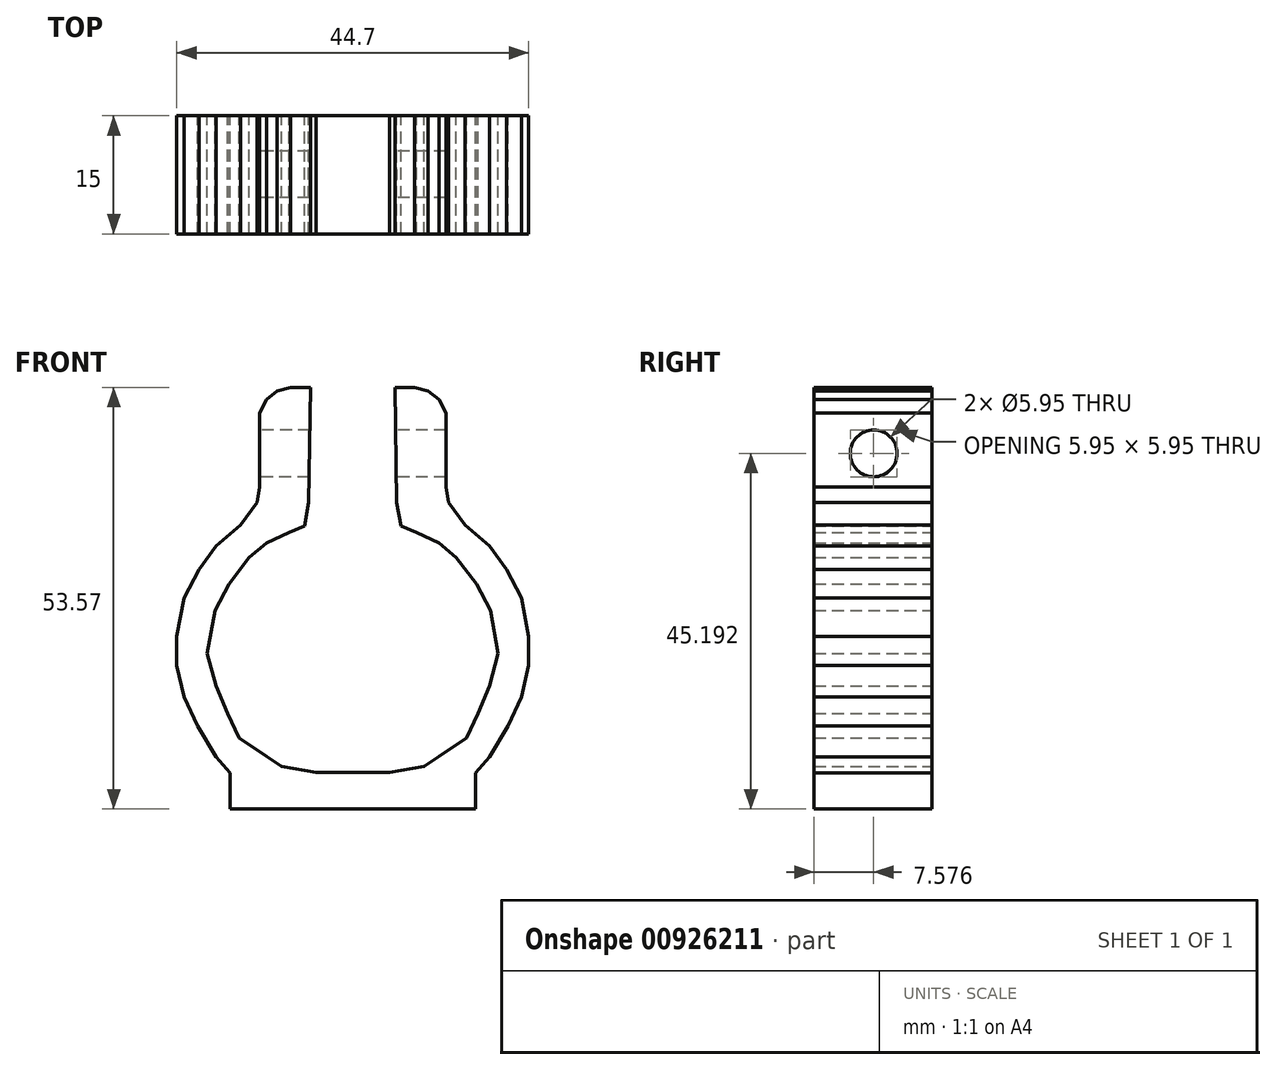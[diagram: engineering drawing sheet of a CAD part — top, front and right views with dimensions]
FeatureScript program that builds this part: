
annotation { "Feature Type Name" : "Feature", "Feature Type Description" : "" }
export const myFeature = defineFeature(function(context is Context, id is Id, definition is map)
    precondition{}
    {
        {
            var Q0;
            Q0=qCreatedBy(makeId("Front.planeOp"),FACE);
            var sketch = newSketch(context, id + "F0", { "sketchPlane" : qUnion([Q0])});
            skLineSegment(sketch, "E0", {"start": v(6.06, 26.73) * mm, "end": v(3.54, 26.73) * mm});
            skLineSegment(sketch, "E1", {"start": v(3.54, 26.73) * mm, "end": v(1.82, 26.27) * mm});
            skLineSegment(sketch, "E2", {"start": v(1.82, 26.27) * mm, "end": v(0.45, 25.22) * mm});
            skLineSegment(sketch, "E3", {"start": v(0.45, 25.22) * mm, "end": v(-0.41, 23.5) * mm});
            skLineSegment(sketch, "E4", {"start": v(-0.41, 23.5) * mm, "end": v(-0.41, 14.1) * mm});
            skLineSegment(sketch, "E5", {"start": v(-0.41, 14.1) * mm, "end": v(-0.77, 12.14) * mm});
            skLineSegment(sketch, "E6", {"start": v(-0.77, 12.14) * mm, "end": v(-2.86, 9.26) * mm});
            skLineSegment(sketch, "E7", {"start": v(-2.86, 9.26) * mm, "end": v(-5.94, 6.6) * mm});
            skLineSegment(sketch, "E8", {"start": v(-5.94, 6.6) * mm, "end": v(-8.14, 3.58) * mm});
            skLineSegment(sketch, "E9", {"start": v(-8.14, 3.58) * mm, "end": v(-10.04, 0) * mm});
            skLineSegment(sketch, "E10", {"start": v(-10.04, 0) * mm, "end": v(-10.94, -4.9) * mm});
            skLineSegment(sketch, "E11", {"start": v(-10.94, -4.9) * mm, "end": v(-10.94, -8.62) * mm});
            skLineSegment(sketch, "E12", {"start": v(-10.94, -8.62) * mm, "end": v(-10.04, -12.58) * mm});
            skLineSegment(sketch, "E13", {"start": v(-10.04, -12.58) * mm, "end": v(-8.29, -16.24) * mm});
            skLineSegment(sketch, "E14", {"start": v(-8.29, -16.24) * mm, "end": v(-5.94, -20.2) * mm});
            skLineSegment(sketch, "E15", {"start": v(-5.94, -20.2) * mm, "end": v(-4.16, -22.27) * mm});
            skLineSegment(sketch, "E16", {"start": v(-4.16, -22.27) * mm, "end": v(-4.16, -26.84) * mm});
            skLineSegment(sketch, "E17", {"start": v(-4.16, -26.84) * mm, "end": v(11.41, -26.84) * mm});
            skLineSegment(sketch, "E18", {"start": v(11.41, -22.19) * mm, "end": v(6.73, -22.19) * mm});
            skLineSegment(sketch, "E19", {"start": v(6.73, -22.19) * mm, "end": v(2.38, -21.4) * mm});
            skLineSegment(sketch, "E20", {"start": v(2.38, -21.4) * mm, "end": v(0.45, -20.13) * mm});
            skLineSegment(sketch, "E21", {"start": v(0.45, -20.13) * mm, "end": v(-3.03, -17.77) * mm});
            skLineSegment(sketch, "E22", {"start": v(-3.03, -17.77) * mm, "end": v(-4.48, -14.72) * mm});
            skLineSegment(sketch, "E23", {"start": v(-4.48, -14.72) * mm, "end": v(-5.94, -11.21) * mm});
            skLineSegment(sketch, "E24", {"start": v(-5.94, -11.21) * mm, "end": v(-7.07, -7.1) * mm});
            skLineSegment(sketch, "E25", {"start": v(-7.07, -7.1) * mm, "end": v(-6.67, -4.92) * mm});
            skLineSegment(sketch, "E26", {"start": v(-6.67, -4.92) * mm, "end": v(-6.07, -1.6) * mm});
            skLineSegment(sketch, "E27", {"start": v(-6.07, -1.6) * mm, "end": v(-4.33, 1.75) * mm});
            skLineSegment(sketch, "E28", {"start": v(-4.33, 1.75) * mm, "end": v(-1.73, 5.1) * mm});
            skLineSegment(sketch, "E29", {"start": v(-1.73, 5.1) * mm, "end": v(0.45, 6.99) * mm});
            skLineSegment(sketch, "E30", {"start": v(0.45, 6.99) * mm, "end": v(3.3, 8.3) * mm});
            skLineSegment(sketch, "E31", {"start": v(3.3, 8.3) * mm, "end": v(5.28, 9.14) * mm});
            skLineSegment(sketch, "E32", {"start": v(5.28, 9.14) * mm, "end": v(5.83, 12.14) * mm});
            skLineSegment(sketch, "E33", {"start": v(11.41, -26.84) * mm, "end": v(11.41, -22.19) * mm});
            skLineSegment(sketch, "E34", {"start": v(11.41, -31.75) * mm, "end": v(11.41, 67.33) * mm});
            skLineSegment(sketch, "E35.MirrorCS", {"start": v(30.96, 3.58) * mm, "end": v(32.86, 0) * mm});
            skLineSegment(sketch, "E36.MirrorCS", {"start": v(29.9, -7.1) * mm, "end": v(29.5, -4.92) * mm});
            skLineSegment(sketch, "E37.MirrorCS", {"start": v(28.76, -20.2) * mm, "end": v(26.98, -22.27) * mm});
            skLineSegment(sketch, "E38.MirrorCS", {"start": v(32.86, 0) * mm, "end": v(33.76, -4.9) * mm});
            skLineSegment(sketch, "E39.MirrorCS", {"start": v(28.9, -1.6) * mm, "end": v(27.15, 1.75) * mm});
            skLineSegment(sketch, "E40.MirrorCS", {"start": v(27.15, 1.75) * mm, "end": v(24.56, 5.1) * mm});
            skLineSegment(sketch, "E41.MirrorCS", {"start": v(29.5, -4.92) * mm, "end": v(28.9, -1.6) * mm});
            skLineSegment(sketch, "E42.MirrorCS", {"start": v(28.76, 6.6) * mm, "end": v(30.96, 3.58) * mm});
            skLineSegment(sketch, "E43.MirrorCS", {"start": v(28.76, -11.21) * mm, "end": v(29.9, -7.1) * mm});
            skLineSegment(sketch, "E44.MirrorCS", {"start": v(22.37, 6.99) * mm, "end": v(19.52, 8.3) * mm});
            skLineSegment(sketch, "E45.MirrorCS", {"start": v(33.76, -4.9) * mm, "end": v(33.76, -8.62) * mm});
            skLineSegment(sketch, "E46.MirrorCS", {"start": v(21, 26.27) * mm, "end": v(22.37, 25.22) * mm});
            skLineSegment(sketch, "E47.MirrorCS", {"start": v(22.37, 25.22) * mm, "end": v(23.24, 23.5) * mm});
            skLineSegment(sketch, "E48.MirrorCS", {"start": v(25.68, 9.26) * mm, "end": v(28.76, 6.6) * mm});
            skLineSegment(sketch, "E49.MirrorCS", {"start": v(23.24, 23.5) * mm, "end": v(23.24, 14.1) * mm});
            skLineSegment(sketch, "E50.MirrorCS", {"start": v(33.76, -8.62) * mm, "end": v(32.86, -12.58) * mm});
            skLineSegment(sketch, "E51.MirrorCS", {"start": v(20.44, -21.4) * mm, "end": v(22.37, -20.13) * mm});
            skLineSegment(sketch, "E52.MirrorCS", {"start": v(23.24, 14.1) * mm, "end": v(23.6, 12.14) * mm});
            skLineSegment(sketch, "E53.MirrorCS", {"start": v(27.3, -14.72) * mm, "end": v(28.76, -11.21) * mm});
            skLineSegment(sketch, "E54.MirrorCS", {"start": v(16.1, -22.19) * mm, "end": v(20.44, -21.4) * mm});
            skLineSegment(sketch, "E55.MirrorCS", {"start": v(32.86, -12.58) * mm, "end": v(31.11, -16.24) * mm});
            skLineSegment(sketch, "E56.MirrorCS", {"start": v(25.85, -17.77) * mm, "end": v(27.3, -14.72) * mm});
            skLineSegment(sketch, "E57.MirrorCS", {"start": v(31.11, -16.24) * mm, "end": v(28.76, -20.2) * mm});
            skLineSegment(sketch, "E58.MirrorCS", {"start": v(26.98, -22.27) * mm, "end": v(26.98, -26.84) * mm});
            skLineSegment(sketch, "E59.MirrorCS", {"start": v(26.98, -26.84) * mm, "end": v(11.41, -26.84) * mm});
            skLineSegment(sketch, "E60.MirrorCS", {"start": v(24.56, 5.1) * mm, "end": v(22.37, 6.99) * mm});
            skLineSegment(sketch, "E61.MirrorCS", {"start": v(22.37, -20.13) * mm, "end": v(25.85, -17.77) * mm});
            skLineSegment(sketch, "E62.MirrorCS", {"start": v(11.41, -22.19) * mm, "end": v(16.1, -22.19) * mm});
            skLineSegment(sketch, "E63.MirrorCS", {"start": v(19.29, 26.73) * mm, "end": v(21, 26.27) * mm});
            skLineSegment(sketch, "E64.MirrorCS", {"start": v(16.76, 26.73) * mm, "end": v(19.29, 26.73) * mm});
            skLineSegment(sketch, "E65.MirrorCS", {"start": v(19.52, 8.3) * mm, "end": v(17.54, 9.14) * mm});
            skLineSegment(sketch, "E66.MirrorCS", {"start": v(17.54, 9.14) * mm, "end": v(17, 12.14) * mm});
            skLineSegment(sketch, "E67.MirrorCS", {"start": v(23.6, 12.14) * mm, "end": v(25.68, 9.26) * mm});
            skLineSegment(sketch, "E68", {"start": v(5.83, 12.14) * mm, "end": v(6.06, 26.73) * mm});
            skLineSegment(sketch, "E69", {"start": v(17, 12.14) * mm, "end": v(16.76, 26.73) * mm});
            skSolve(sketch);
        }
        {
            var Q0;
            Q0 = qSketchRegion(id + "F0", true);
            extrude(context, id + "F1", {"entities" : qUnion([Q0]), "endBound" : BoundingType.SYMMETRIC, "depth" : 15 * mm, "offsetDistance" : 25 * mm});
        }
        {
            var Q0;
            Q0=qCreatedBy(makeId("Right.planeOp"),FACE);
            var sketch = newSketch(context, id + "F2", { "sketchPlane" : qUnion([Q0])});
            skCircle(sketch, "E70", {"center": v(0.08, 18.35) * mm, "radius": 2.97 * mm});
            skPoint(sketch, "E70.first.point", {"position": v(2.84, 17.25) * mm});
            skPoint(sketch, "E70.second.point", {"position": v(-2.74, 17.38) * mm});
            skPoint(sketch, "E70.third.point", {"position": v(0, 21.33) * mm});
            skSolve(sketch);
        }
        {
            var Q0;
            Q0 = qSketchRegion(id + "F2", true);
            extrude(context, id + "F3", {"entities" : qUnion([Q0]), "operationType" : NewBodyOperationType.REMOVE, "endBound" : BoundingType.THROUGH_ALL, "depth" : 0 * mm, "offsetDistance" : 25 * mm});
        }
        {
            var Q0;
            Q0=makeQuery(id+"F3.boolean.opBoolean","COPY",FACE,{"derivedFrom":makeQuery(id+"F3.opExtrude","CAP_FACE",FACE,{"disambiguationData":[OSD([sQuery(id+"F2.wireOp",EDGE,"E70")])],"isStart":true})});
            var sketch = newSketch(context, id + "F4", { "sketchPlane" : qUnion([Q0])});
            skCircle(sketch, "E71", {"center": v(0.08, 18.35) * mm, "radius": 2.97 * mm});
            skPoint(sketch, "E71.first.point", {"position": v(3.02, 18.79) * mm});
            skPoint(sketch, "E71.second.point", {"position": v(0, 15.38) * mm});
            skPoint(sketch, "E71.third.point", {"position": v(-2.84, 18.94) * mm});
            skSolve(sketch);
        }
        {
            var Q0;
            Q0 = qSketchRegion(id + "F4", true);
            extrude(context, id + "F5", {"entities" : qUnion([Q0]), "operationType" : NewBodyOperationType.REMOVE, "endBound" : BoundingType.THROUGH_ALL, "oppositeDirection" : true, "depth" : 25 * mm, "offsetDistance" : 25 * mm});
        }
    });
